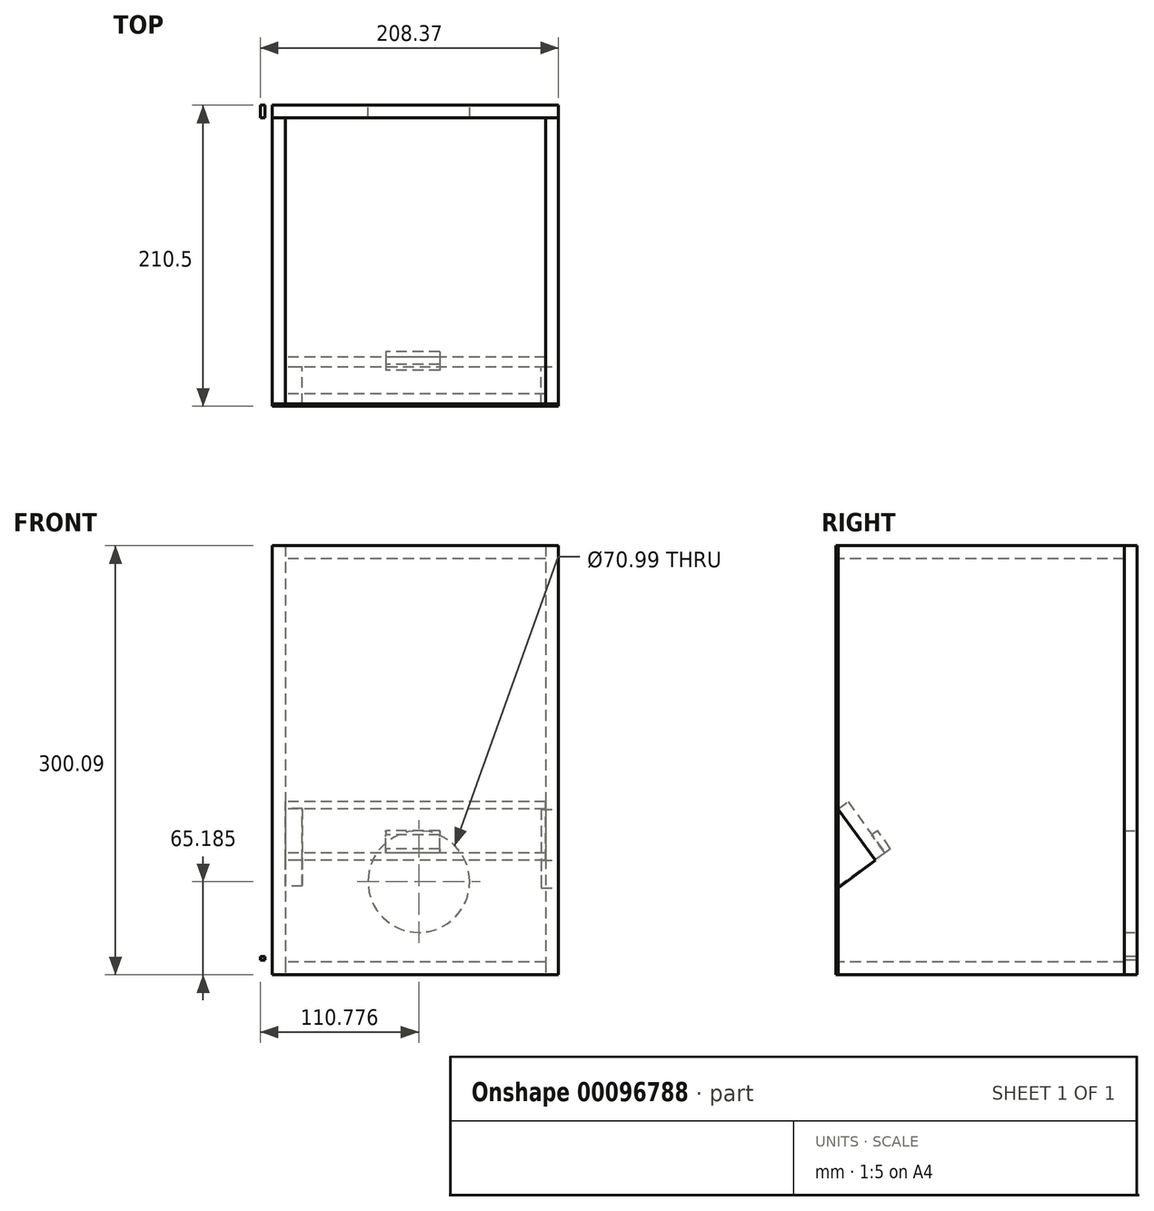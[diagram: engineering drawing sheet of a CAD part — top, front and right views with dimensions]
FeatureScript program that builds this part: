
annotation { "Feature Type Name" : "Feature", "Feature Type Description" : "" }
export const myFeature = defineFeature(function(context is Context, id is Id, definition is map)
    precondition{}
    {
        {
            var Q0;
            Q0=qCreatedBy(makeId("Front.planeOp"),FACE);
            var sketch = newSketch(context, id + "F0", { "sketchPlane" : qUnion([Q0])});
            skLineSegment(sketch, "E0.bottom", {"start": v(0, -16.48) * mm, "end": v(200, -16.48) * mm});
            skLineSegment(sketch, "E0.top", {"start": v(0, 283.52) * mm, "end": v(200, 283.52) * mm});
            skLineSegment(sketch, "E0.left", {"start": v(0, -16.48) * mm, "end": v(0, 283.52) * mm});
            skLineSegment(sketch, "E0.right", {"start": v(200, -16.48) * mm, "end": v(200, 283.52) * mm});
            skSolve(sketch);
        }
        {
            var Q0;
            Q0 = qSketchRegion(id + "F0", true);
            extrude(context, id + "F1", {"entities" : qUnion([Q0]), "depth" : 1.5 * mm});
        }
        {
            var Q0;
            Q0=makeQuery(id+"F1.opExtrude","CAP_FACE",FACE,{"disambiguationData":[OSD([sQuery(id+"F0.wireOp",EDGE,"E0.bottom"),sQuery(id+"F0.wireOp",EDGE,"E0.top"),sQuery(id+"F0.wireOp",EDGE,"E0.left"),sQuery(id+"F0.wireOp",EDGE,"E0.right")])],"isStart":true});
            var sketch = newSketch(context, id + "F2", { "sketchPlane" : qUnion([Q0])});
            skLineSegment(sketch, "E1.bottom", {"start": v(0, 283.52) * mm, "end": v(-9, 283.52) * mm});
            skLineSegment(sketch, "E1.top", {"start": v(0, -16.48) * mm, "end": v(-9, -16.48) * mm});
            skLineSegment(sketch, "E1.left", {"start": v(0, 283.52) * mm, "end": v(0, -16.48) * mm});
            skLineSegment(sketch, "E1.right", {"start": v(-9, 283.52) * mm, "end": v(-9, -16.48) * mm});
            skSolve(sketch);
        }
        {
            var Q0;
            Q0 = qSketchRegion(id + "F2", true);
            extrude(context, id + "F3", {"entities" : qUnion([Q0]), "depth" : 200 * mm});
        }
        {
            var Q0;
            Q0=makeQuery(id+"F3.opExtrude","SWEPT_FACE",FACE,{"disambiguationData":[OSD([sQuery(id+"F2.wireOp",EDGE,"E1.right")])]});
            var sketch = newSketch(context, id + "F4", { "sketchPlane" : qUnion([Q0])});
            skLineSegment(sketch, "E2", {"start": v(0, 99.6) * mm, "end": v(0, 45.51) * mm});
            skLineSegment(sketch, "E3", {"start": v(0, 45.51) * mm, "end": v(25.7, 63.7) * mm});
            skLineSegment(sketch, "E4", {"start": v(25.7, 63.7) * mm, "end": v(0, 99.6) * mm});
            skSolve(sketch);
        }
        {
            var Q0;
            Q0 = qSketchRegion(id + "F4", true);
            extrude(context, id + "F5", {"entities" : qUnion([Q0]), "depth" : 12 * mm});
        }
        {
            var Q0;
            Q0=makeQuery(id+"F3.opExtrude","SWEPT_FACE",FACE,{"disambiguationData":[OSD([sQuery(id+"F2.wireOp",EDGE,"E1.right")])]});
            var sketch = newSketch(context, id + "F6", { "sketchPlane" : qUnion([Q0])});
            skLineSegment(sketch, "E5", {"start": v(25.7, 63.7) * mm, "end": v(0, 99.55) * mm});
            skLineSegment(sketch, "E6", {"start": v(0, 99.55) * mm, "end": v(7, 104.56) * mm});
            skLineSegment(sketch, "E7", {"start": v(7, 104.56) * mm, "end": v(32.69, 68.7) * mm});
            skLineSegment(sketch, "E8", {"start": v(32.69, 68.7) * mm, "end": v(25.7, 63.7) * mm});
            skSolve(sketch);
        }
        {
            var Q0;
            Q0 = qSketchRegion(id + "F6", true);
            extrude(context, id + "F7", {"entities" : qUnion([Q0]), "depth" : 182 * mm});
        }
        {
            var Q0;
            Q0=makeQuery(id+"F7.opExtrude","SWEPT_FACE",FACE,{"disambiguationData":[OSD([sQuery(id+"F6.wireOp",EDGE,"E7")])]});
            var sketch = newSketch(context, id + "F8", { "sketchPlane" : qUnion([Q0])});
            skLineSegment(sketch, "E9.bottom", {"start": v(-117.04, 36.8) * mm, "end": v(-79.35, 36.8) * mm});
            skLineSegment(sketch, "E9.top", {"start": v(-117.04, 52.33) * mm, "end": v(-79.35, 52.33) * mm});
            skLineSegment(sketch, "E9.left", {"start": v(-117.04, 36.8) * mm, "end": v(-117.04, 52.33) * mm});
            skLineSegment(sketch, "E9.right", {"start": v(-79.35, 36.8) * mm, "end": v(-79.35, 52.33) * mm});
            skSolve(sketch);
        }
        {
            var Q0;
            Q0 = qSketchRegion(id + "F8", true);
            extrude(context, id + "F9", {"entities" : qUnion([Q0]), "depth" : 5 * mm});
        }
        {
            var Q0;
            Q0=makeQuery(id+"F3.opExtrude","SWEPT_FACE",FACE,{"disambiguationData":[OSD([sQuery(id+"F2.wireOp",EDGE,"E1.right")])]});
            var sketch = newSketch(context, id + "F10", { "sketchPlane" : qUnion([Q0])});
            skLineSegment(sketch, "E10.bottom", {"start": v(200, 283.52) * mm, "end": v(0, 283.52) * mm});
            skLineSegment(sketch, "E10.top", {"start": v(200, 274.52) * mm, "end": v(0, 274.52) * mm});
            skLineSegment(sketch, "E10.left", {"start": v(200, 283.52) * mm, "end": v(200, 274.52) * mm});
            skLineSegment(sketch, "E10.right", {"start": v(0, 283.52) * mm, "end": v(0, 274.52) * mm});
            skSolve(sketch);
        }
        {
            var Q0;
            Q0 = qSketchRegion(id + "F10", true);
            extrude(context, id + "F11", {"entities" : qUnion([Q0]), "depth" : 182 * mm});
        }
        {
            var Q0;
            Q0=makeQuery(id+"F3.opExtrude","SWEPT_FACE",FACE,{"disambiguationData":[OSD([sQuery(id+"F2.wireOp",EDGE,"E1.right")])]});
            var sketch = newSketch(context, id + "F12", { "sketchPlane" : qUnion([Q0])});
            skLineSegment(sketch, "E11.bottom", {"start": v(200, -16.48) * mm, "end": v(0, -16.48) * mm});
            skLineSegment(sketch, "E11.top", {"start": v(200, -7.48) * mm, "end": v(0, -7.48) * mm});
            skLineSegment(sketch, "E11.left", {"start": v(200, -16.48) * mm, "end": v(200, -7.48) * mm});
            skLineSegment(sketch, "E11.right", {"start": v(0, -16.48) * mm, "end": v(0, -7.48) * mm});
            skSolve(sketch);
        }
        {
            var Q0;
            Q0 = qSketchRegion(id + "F12", true);
            extrude(context, id + "F13", {"entities" : qUnion([Q0]), "depth" : 182 * mm});
        }
        {
            var Q0;
            Q0=makeQuery(id+"F11.opExtrude","CAP_FACE",FACE,{"disambiguationData":[OSD([sQuery(id+"F10.wireOp",EDGE,"E10.bottom"),sQuery(id+"F10.wireOp",EDGE,"E10.top"),sQuery(id+"F10.wireOp",EDGE,"E10.left"),sQuery(id+"F10.wireOp",EDGE,"E10.right")])],"isStart":false});
            var sketch = newSketch(context, id + "F14", { "sketchPlane" : qUnion([Q0])});
            skLineSegment(sketch, "E12.bottom", {"start": v(200, 283.52) * mm, "end": v(0, 283.52) * mm});
            skLineSegment(sketch, "E12.top", {"start": v(200, -16.57) * mm, "end": v(0, -16.57) * mm});
            skLineSegment(sketch, "E12.left", {"start": v(200, 283.52) * mm, "end": v(200, -16.57) * mm});
            skLineSegment(sketch, "E12.right", {"start": v(0, 283.52) * mm, "end": v(0, -16.57) * mm});
            skSolve(sketch);
        }
        {
            var Q0;
            Q0 = qSketchRegion(id + "F14", true);
            extrude(context, id + "F15", {"entities" : qUnion([Q0]), "depth" : 9 * mm});
        }
        {
            var Q0;
            Q0=makeQuery(id+"F15.opExtrude","SWEPT_FACE",FACE,{"disambiguationData":[OSD([sQuery(id+"F14.wireOp",EDGE,"E12.left")])]});
            var sketch = newSketch(context, id + "F16", { "sketchPlane" : qUnion([Q0])});
            skLineSegment(sketch, "E13.bottom", {"start": v(-200, 283.52) * mm, "end": v(0, 283.52) * mm});
            skLineSegment(sketch, "E13.top", {"start": v(-200, -16.48) * mm, "end": v(0, -16.48) * mm});
            skLineSegment(sketch, "E13.left", {"start": v(-200, 283.52) * mm, "end": v(-200, -16.48) * mm});
            skLineSegment(sketch, "E13.right", {"start": v(0, 283.52) * mm, "end": v(0, -16.48) * mm});
            skLineSegment(sketch, "E14.bottom", {"start": v(5.08, -3.72) * mm, "end": v(8.37, -3.72) * mm});
            skLineSegment(sketch, "E14.top", {"start": v(5.08, -6.3) * mm, "end": v(8.37, -6.3) * mm});
            skLineSegment(sketch, "E14.left", {"start": v(5.08, -3.72) * mm, "end": v(5.08, -6.3) * mm});
            skLineSegment(sketch, "E14.right", {"start": v(8.37, -3.72) * mm, "end": v(8.37, -6.3) * mm});
            skSolve(sketch);
        }
        {
            var Q0;
            Q0 = qSketchRegion(id + "F16", true);
            extrude(context, id + "F17", {"entities" : qUnion([Q0]), "depth" : 9 * mm});
        }
        {
            var Q0;
            Q0=makeQuery(id+"F17.opExtrude","CAP_FACE",FACE,{"disambiguationData":[OSD([sQuery(id+"F16.wireOp",EDGE,"E13.bottom"),sQuery(id+"F16.wireOp",EDGE,"E13.top"),sQuery(id+"F16.wireOp",EDGE,"E13.left"),sQuery(id+"F16.wireOp",EDGE,"E13.right")])],"isStart":false});
            var sketch = newSketch(context, id + "F18", { "sketchPlane" : qUnion([Q0])});
            skCircle(sketch, "E15", {"center": v(-102.4, 48.61) * mm, "radius": 35.5 * mm});
            skSolve(sketch);
        }
        {
            var Q0;
            Q0 = qSketchRegion(id + "F18", true);
            extrude(context, id + "F19", {"entities" : qUnion([Q0]), "operationType" : NewBodyOperationType.REMOVE, "oppositeDirection" : true, "depth" : 9 * mm});
        }
        {
            var Q0;
            Q0=makeQuery(id+"F15.opExtrude","CAP_FACE",FACE,{"disambiguationData":[OSD([sQuery(id+"F14.wireOp",EDGE,"E12.bottom"),sQuery(id+"F14.wireOp",EDGE,"E12.top"),sQuery(id+"F14.wireOp",EDGE,"E12.left"),sQuery(id+"F14.wireOp",EDGE,"E12.right")])],"isStart":false});
            var sketch = newSketch(context, id + "F20", { "sketchPlane" : qUnion([Q0])});
            skLineSegment(sketch, "E16", {"start": v(0, 99.16) * mm, "end": v(26.2, 63.47) * mm});
            skLineSegment(sketch, "E17", {"start": v(26.2, 63.47) * mm, "end": v(0, 44.23) * mm});
            skLineSegment(sketch, "E18", {"start": v(0, 44.23) * mm, "end": v(0, 99.16) * mm});
            skSolve(sketch);
        }
        {
            var Q0;
            Q0 = qSketchRegion(id + "F20", true);
            extrude(context, id + "F21", {"entities" : qUnion([Q0]), "oppositeDirection" : true, "depth" : 12 * mm});
        }
    });
